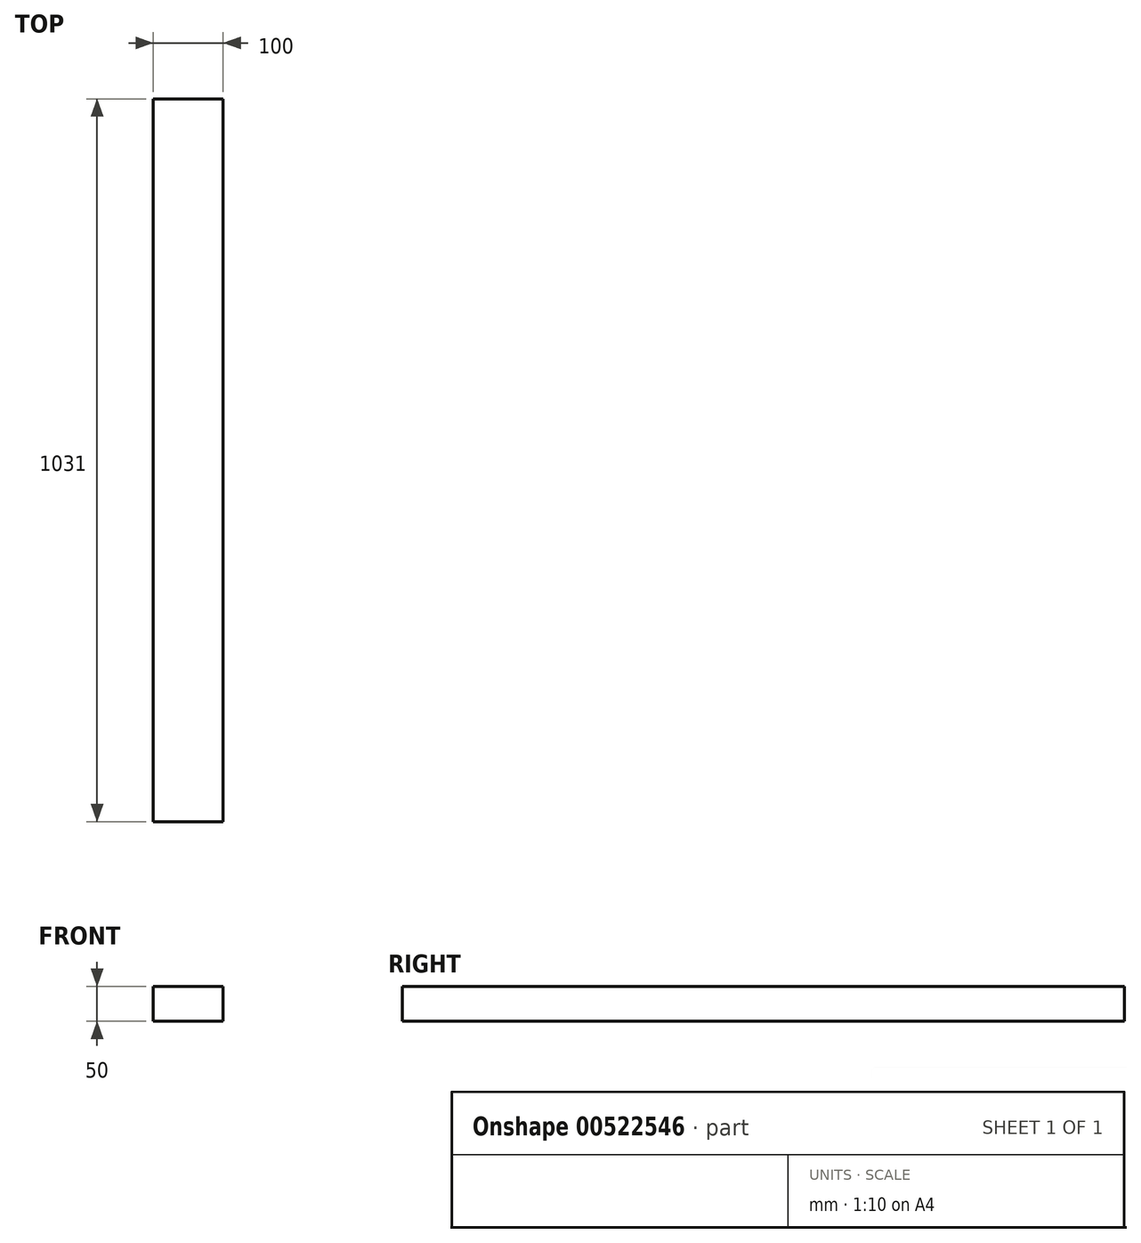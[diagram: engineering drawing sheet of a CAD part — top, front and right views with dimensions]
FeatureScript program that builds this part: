
annotation { "Feature Type Name" : "Feature", "Feature Type Description" : "" }
export const myFeature = defineFeature(function(context is Context, id is Id, definition is map)
    precondition{}
    {
        {
            var Q0;
            Q0=qCreatedBy(makeId("Front.planeOp"),FACE);
            var sketch = newSketch(context, id + "F0", { "sketchPlane" : qUnion([Q0])});
            skLineSegment(sketch, "E0.bottom", {"start": v(-139.39, 44.33) * mm, "end": v(-39.39, 44.33) * mm});
            skLineSegment(sketch, "E0.top", {"start": v(-139.39, -5.67) * mm, "end": v(-39.39, -5.67) * mm});
            skLineSegment(sketch, "E0.left", {"start": v(-139.39, 44.33) * mm, "end": v(-139.39, -5.67) * mm});
            skLineSegment(sketch, "E0.right", {"start": v(-39.39, 44.33) * mm, "end": v(-39.39, -5.67) * mm});
            skSolve(sketch);
        }
        {
            var Q0;
            Q0=qSketchRegion(id+"F0",true);
            extrude(context, id + "F1", {"entities" : qUnion([Q0]), "depth" : 1031 * mm, "offsetDistance" : 25 * mm});
        }
    });
